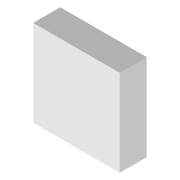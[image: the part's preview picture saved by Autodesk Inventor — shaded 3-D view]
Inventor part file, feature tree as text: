
AUTODESK INVENTOR PART (.ipt)
format: ipt  version: 2022 (Build 260153000, 153)  size: 74,752 bytes
history: native  units: mm
features: extrude x1, sketch x1
ambient origin geometry x8: Origin, YZ Plane, XZ Plane, XY Plane, X Axis, Y Axis, Z Axis, Center Point
bodies: Solid1 (feature_tree)
feature tree (2):
  extrude  "Extrusion1"  Depth=6.4mm
  sketch  "Sketch1"  dims[d0=6.4mm d1=6.4mm d2=2.0mm d3=0.0mm]
